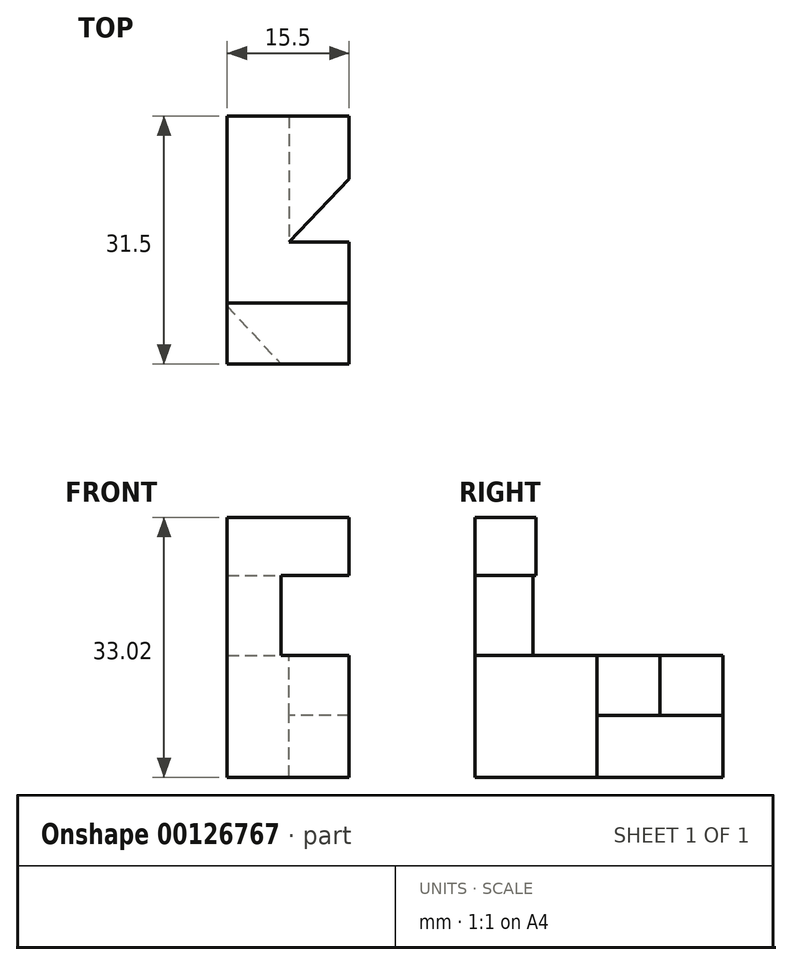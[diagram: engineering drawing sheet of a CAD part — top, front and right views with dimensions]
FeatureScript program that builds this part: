
annotation { "Feature Type Name" : "Feature", "Feature Type Description" : "" }
export const myFeature = defineFeature(function(context is Context, id is Id, definition is map)
    precondition{}
    {
        {
            var Q0;
            Q0=qCreatedBy(makeId("Top.planeOp"),FACE);
            var sketch = newSketch(context, id + "F0", { "sketchPlane" : qUnion([Q0])});
            skLineSegment(sketch, "E0.bottom", {"start": v(7.75, 7.75) * mm, "end": v(-7.75, 7.75) * mm});
            skLineSegment(sketch, "E0.top", {"start": v(7.75, -7.75) * mm, "end": v(-7.75, -7.75) * mm});
            skLineSegment(sketch, "E0.left", {"start": v(7.75, 7.75) * mm, "end": v(7.75, -7.75) * mm});
            skLineSegment(sketch, "E0.right", {"start": v(-7.75, 7.75) * mm, "end": v(-7.75, -7.75) * mm});
            skPoint(sketch, "E0.middle", {"position": v(0, 0) * mm});
            skSolve(sketch);
        }
        {
            var Q0;
            Q0=makeQuery(id+"F0.imprint","IMPRINT",FACE,{"disambiguationData":[TD([[makeQuery(id+"F0.imprint","IMPRINT",EDGE,{"derivedFrom":sQuery(id+"F0.wireOp",EDGE,"E0.bottom")}),1.0]])]});
            extrude(context, id + "F1", {"entities" : qUnion([Q0]), "endBound" : BoundingType.SYMMETRIC, "depth" : 15.5 * mm});
        }
        {
            var Q0;
            Q0=makeQuery(id+"F1.opExtrude","CAP_FACE",FACE,{"disambiguationData":[OSD([sQuery(id+"F0.wireOp",EDGE,"E0.bottom"),sQuery(id+"F0.wireOp",EDGE,"E0.top"),sQuery(id+"F0.wireOp",EDGE,"E0.left"),sQuery(id+"F0.wireOp",EDGE,"E0.right")])],"isStart":false});
            var sketch = newSketch(context, id + "F2", { "sketchPlane" : qUnion([Q0])});
            skLineSegment(sketch, "E1", {"start": v(-7.75, -7.75) * mm, "end": v(-7.75, -0.38) * mm});
            skLineSegment(sketch, "E2", {"start": v(-7.75, -7.75) * mm, "end": v(-0.9, -7.75) * mm});
            skLineSegment(sketch, "E3", {"start": v(-7.75, -0.38) * mm, "end": v(-0.9, -7.75) * mm});
            skSolve(sketch);
        }
        {
            var Q0;
            Q0=makeQuery(id+"F2.imprint","IMPRINT",FACE,{"disambiguationData":[TD([[makeQuery(id+"F2.imprint","IMPRINT",EDGE,{"derivedFrom":sQuery(id+"F2.wireOp",EDGE,"E1")}),1.0]])]});
            extrude(context, id + "F3", {"entities" : qUnion([Q0]), "operationType" : NewBodyOperationType.ADD, "depth" : 10.16 * mm});
        }
        {
            var Q0;
            Q0=makeQuery(id+"F3.opExtrude","CAP_FACE",FACE,{"disambiguationData":[OSD([sQuery(id+"F2.wireOp",EDGE,"E1"),sQuery(id+"F2.wireOp",EDGE,"E2"),sQuery(id+"F2.wireOp",EDGE,"E3")])],"isStart":false});
            var sketch = newSketch(context, id + "F4", { "sketchPlane" : qUnion([Q0])});
            skLineSegment(sketch, "E4.0", {"start": v(7.75, 7.75) * mm, "end": v(7.75, -7.75) * mm});
            skLineSegment(sketch, "E5", {"start": v(7.75, -7.75) * mm, "end": v(-7.75, -7.75) * mm});
            skLineSegment(sketch, "E6", {"start": v(-7.75, -7.75) * mm, "end": v(-7.75, 0) * mm});
            skLineSegment(sketch, "E7", {"start": v(-7.75, 0) * mm, "end": v(7.75, 0) * mm});
            skSolve(sketch);
        }
        {
            var Q0;
            Q0 = qSketchRegion(id + "F4", true);
            extrude(context, id + "F5", {"entities" : qUnion([Q0]), "operationType" : NewBodyOperationType.ADD, "depth" : 7.37 * mm});
        }
        {
            var Q0;
            Q0=makeQuery(id+"F1.opExtrude","SWEPT_FACE",FACE,{"disambiguationData":[OSD([sQuery(id+"F0.wireOp",EDGE,"E0.bottom")])]});
            var sketch = newSketch(context, id + "F6", { "sketchPlane" : qUnion([Q0])});
            skLineSegment(sketch, "E8", {"start": v(7.75, -7.75) * mm, "end": v(-0.12, -7.75) * mm});
            skLineSegment(sketch, "E9", {"start": v(-0.12, -7.75) * mm, "end": v(-0.12, 7.75) * mm});
            skLineSegment(sketch, "E10", {"start": v(-0.12, 7.75) * mm, "end": v(7.75, 7.75) * mm});
            skLineSegment(sketch, "E11", {"start": v(7.75, 7.75) * mm, "end": v(7.75, -7.75) * mm});
            skSolve(sketch);
        }
        {
            var Q0;
            Q0=makeQuery(id+"F6.imprint","IMPRINT",FACE,{"disambiguationData":[TD([[makeQuery(id+"F6.imprint","IMPRINT",EDGE,{"derivedFrom":sQuery(id+"F6.wireOp",EDGE,"E8")}),1.0]])]});
            extrude(context, id + "F7", {"entities" : qUnion([Q0]), "operationType" : NewBodyOperationType.ADD, "depth" : 16 * mm});
        }
        {
            var Q0;
            Q0=makeQuery(id+"F7.opExtrude","SWEPT_FACE",FACE,{"disambiguationData":[OSD([sQuery(id+"F6.wireOp",EDGE,"E9")])]});
            var sketch = newSketch(context, id + "F8", { "sketchPlane" : qUnion([Q0])});
            skLineSegment(sketch, "E12", {"start": v(23.75, 7.75) * mm, "end": v(23.75, 0.13) * mm});
            skLineSegment(sketch, "E13", {"start": v(23.75, 0.13) * mm, "end": v(7.75, 0.13) * mm});
            skLineSegment(sketch, "E14", {"start": v(15.75, 0.13) * mm, "end": v(15.75, 7.75) * mm});
            skSolve(sketch);
        }
        {
            var Q0;
            Q0 = qSketchRegion(id + "F8", true);
            var Q1;
            {var subQ0=sQuery(id+"F8.wireOp",EDGE,"E12");Q1=makeQuery(id+"F8.imprint","IMPRINT",FACE,{"disambiguationData":[TD([[makeQuery(id+"F8.imprint","IMPRINT",EDGE,{"derivedFrom":subQ0}),1.0]])]});}
            extrude(context, id + "F9", {"entities" : qUnion([Q0, Q1]), "operationType" : NewBodyOperationType.ADD, "depth" : 7.62 * mm});
        }
        {
            var Q0;
            {var subQ0=sQuery(id+"F6.wireOp",EDGE,"E10");var subQ1=sQuery(id+"F0.wireOp",EDGE,"E0.bottom");Q0=makeQuery(id+"F9.boolean.opBoolean","MERGE",FACE,{"derivedFrom":[makeQuery(id+"F7.boolean.opBoolean","MERGE",FACE,{"derivedFrom":[makeQuery(id+"F1.opExtrude","CAP_FACE",FACE,{"disambiguationData":[OSD([subQ1,sQuery(id+"F0.wireOp",EDGE,"E0.top"),sQuery(id+"F0.wireOp",EDGE,"E0.left"),sQuery(id+"F0.wireOp",EDGE,"E0.right")])],"isStart":false}),makeQuery(id+"F7.opExtrude","SWEPT_FACE",FACE,{"disambiguationData":[OSD([subQ0])]})]}),makeQuery(id+"F9.opExtrude","SWEPT_FACE",FACE,{"disambiguationData":[OSD([subQ1,sQuery(id+"F6.wireOp",EDGE,"E9"),subQ0])]})]});}
            var sketch = newSketch(context, id + "F10", { "sketchPlane" : qUnion([Q0])});
            skLineSegment(sketch, "E15.0", {"start": v(7.74, 15.75) * mm, "end": v(0.12, 15.75) * mm});
            skLineSegment(sketch, "E16.0", {"start": v(0.12, 15.75) * mm, "end": v(0.12, 7.75) * mm});
            skLineSegment(sketch, "E17", {"start": v(7.74, 15.75) * mm, "end": v(0.12, 7.75) * mm});
            skSolve(sketch);
        }
        {
            var Q0;
            Q0=makeQuery(id+"F10.imprint","IMPRINT",FACE,{"disambiguationData":[TD([[makeQuery(id+"F10.imprint","IMPRINT",EDGE,{"derivedFrom":sQuery(id+"F10.wireOp",EDGE,"E15.0")}),1.0]])]});
            extrude(context, id + "F11", {"entities" : qUnion([Q0]), "operationType" : NewBodyOperationType.ADD, "oppositeDirection" : true, "depth" : 7.62 * mm});
        }
    });
